# Revit family: URA SPOT Standard - Non Permanent-ENG
name_source: partatom
category: Luminaires
units: mm (PartAtom-declared; Revit-internal decimal feet)

## family parameters
Cote de connecteur circulaire = Utiliser le diamètre
Couper avec des vides une fois chargée = Non
Hôte = Face
Partagée = Non
Repere pour localisation dans la piece = Non
Source d'éclairage = Non
Type d'élément = Normal

## types (1)
- 100LM-1H
    Autonomy = 1H
    Color = White
    Connected Object = Non
    Connection type = Screw connection
    Control system = without
    Diameter = 125 mm
    Elévation par défaut = 2300 mm
    Emergency power supply = Autonomous (individual battery)
    Fabricant = LEGRAND
    Frequency = 50-60
    Function = Escape and mood lighting
    General Conditions of Use = https://export.legrand.com
    Height = 45 mm
    IK = 07
    IP = 42
    Installation method = Flush-mounting
    Material = Plastic
    Operating temperature MIN-MAX = -5-35
    Pictogram type = other
    Power supply = 230 AC/DC
    Product designation = EMERGENCY LIGHT U22ROUND FLUSH NON PERMANENT 100 LUMENS 1H STANDARD
    Protection class = II
    Recessed height = 42 mm
    Reference = LG-660032
    Spare battery = 660180
    Standby consumption = 0.0 mA
    Switching type = Non permanent
    System power = 1 W
    URL = https://www.legrand.com
    Useful luminous flux = 100 lm
    battery status = NiCd
    light source = LED not exchangeable
    terminal capacity = 1,5-2,5
